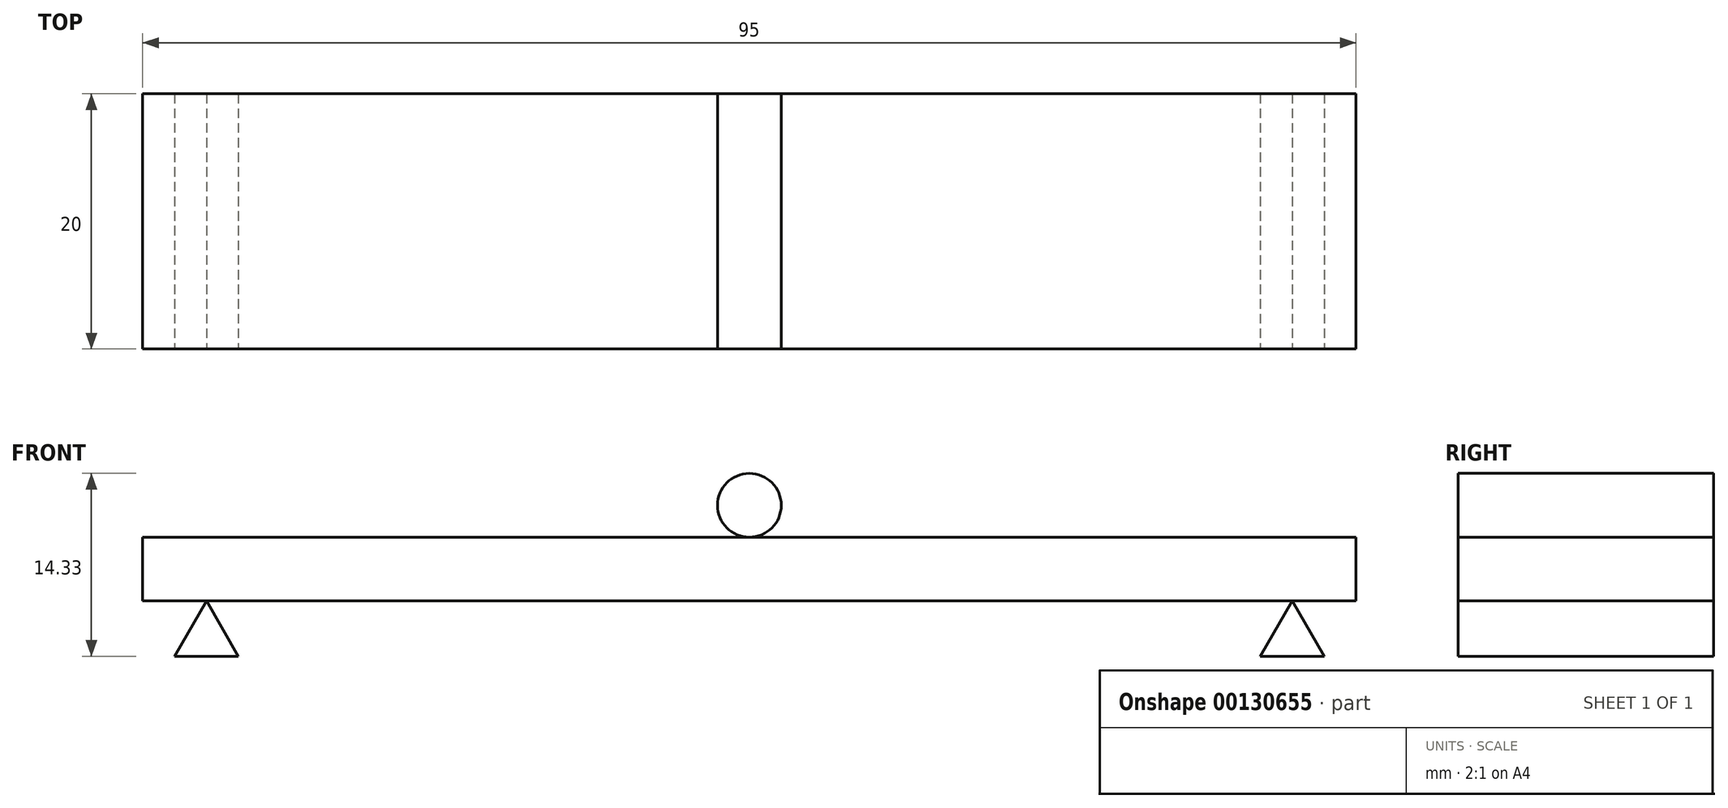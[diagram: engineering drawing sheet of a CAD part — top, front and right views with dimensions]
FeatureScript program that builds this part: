
annotation { "Feature Type Name" : "Feature", "Feature Type Description" : "" }
export const myFeature = defineFeature(function(context is Context, id is Id, definition is map)
    precondition{}
    {
        {
            var Q0;
            Q0=qCreatedBy(makeId("Front.planeOp"),FACE);
            var sketch = newSketch(context, id + "F0", { "sketchPlane" : qUnion([Q0])});
            skLineSegment(sketch, "E0.bottom", {"start": v(47.5, 2.5) * mm, "end": v(-47.5, 2.5) * mm});
            skLineSegment(sketch, "E0.top", {"start": v(47.5, -2.5) * mm, "end": v(-47.5, -2.5) * mm});
            skLineSegment(sketch, "E0.left", {"start": v(47.5, 2.5) * mm, "end": v(47.5, -2.5) * mm});
            skLineSegment(sketch, "E0.right", {"start": v(-47.5, 2.5) * mm, "end": v(-47.5, -2.5) * mm});
            skPoint(sketch, "E0.middle", {"position": v(0, 0) * mm});
            skSolve(sketch);
        }
        {
            var Q0;
            Q0=makeQuery(id+"F0.imprint","IMPRINT",FACE,{"disambiguationData":[TD([[makeQuery(id+"F0.imprint","IMPRINT",EDGE,{"derivedFrom":sQuery(id+"F0.wireOp",EDGE,"E0.bottom")}),1.0]])]});
            extrude(context, id + "F1", {"entities" : qUnion([Q0]), "oppositeDirection" : true, "depth" : 20 * mm});
        }
        {
            var Q0;
            Q0=makeQuery(id+"F1.opExtrude","CAP_FACE",FACE,{"disambiguationData":[OSD([sQuery(id+"F0.wireOp",EDGE,"E0.bottom"),sQuery(id+"F0.wireOp",EDGE,"E0.top"),sQuery(id+"F0.wireOp",EDGE,"E0.left"),sQuery(id+"F0.wireOp",EDGE,"E0.right")])],"isStart":true});
            var sketch = newSketch(context, id + "F2", { "sketchPlane" : qUnion([Q0])});
            skSolve(sketch);
        }
        {
            var Q0;
            Q0=makeQuery(id+"F2.imprint","IMPRINT",FACE,{"disambiguationData":[TD([[makeQuery(id+"F2.imprint","IMPRINT",EDGE,{"derivedFrom":makeQuery(id+"F1.opExtrude","CAP_EDGE",EDGE,{"disambiguationData":[OSD([sQuery(id+"F0.wireOp",EDGE,"E0.bottom")])],"isStart":true})}),1.0]])]});
            var sketch = newSketch(context, id + "F3", { "sketchPlane" : qUnion([Q0])});
            skCircle(sketch, "E1", {"center": v(0, 5) * mm, "radius": 2.5 * mm});
            skSolve(sketch);
        }
        {
            var Q0;
            Q0=makeQuery(id+"F3.imprint","IMPRINT",FACE,{"disambiguationData":[TD([[makeQuery(id+"F3.imprint","IMPRINT",EDGE,{"derivedFrom":sQuery(id+"F3.wireOp",EDGE,"E1")}),1.0]])]});
            extrude(context, id + "F4", {"entities" : qUnion([Q0]), "operationType" : NewBodyOperationType.ADD, "oppositeDirection" : true, "depth" : 20 * mm});
        }
        {
            var Q0;
            Q0=qCreatedBy(makeId("Front.planeOp"),FACE);
            var sketch = newSketch(context, id + "F5", { "sketchPlane" : qUnion([Q0])});
            skLineSegment(sketch, "E2.0", {"start": v(-40, -6.83) * mm, "end": v(-45, -6.83) * mm});
            skLineSegment(sketch, "E2.1", {"start": v(-45, -6.83) * mm, "end": v(-42.5, -2.5) * mm});
            skLineSegment(sketch, "E2.2", {"start": v(-42.5, -2.5) * mm, "end": v(-40, -6.83) * mm});
            skPoint(sketch, "E2.0.midPoint", {"position": v(-42.5, -6.83) * mm});
            skLineSegment(sketch, "E3.0", {"start": v(45, -6.83) * mm, "end": v(40, -6.83) * mm});
            skLineSegment(sketch, "E3.1", {"start": v(40, -6.83) * mm, "end": v(42.5, -2.5) * mm});
            skLineSegment(sketch, "E3.2", {"start": v(42.5, -2.5) * mm, "end": v(45, -6.83) * mm});
            skPoint(sketch, "E3.0.midPoint", {"position": v(42.5, -6.83) * mm});
            skSolve(sketch);
        }
        {
            var Q0;
            Q0=makeQuery(id+"F5.imprint","IMPRINT",FACE,{"disambiguationData":[TD([[makeQuery(id+"F5.imprint","IMPRINT",EDGE,{"derivedFrom":sQuery(id+"F5.wireOp",EDGE,"E2.0")}),-1.0]])]});
            extrude(context, id + "F6", {"entities" : qUnion([Q0]), "oppositeDirection" : true, "depth" : 20 * mm});
        }
        {
            var Q0;
            Q0=makeQuery(id+"F5.imprint","IMPRINT",FACE,{"disambiguationData":[TD([[makeQuery(id+"F5.imprint","IMPRINT",EDGE,{"derivedFrom":sQuery(id+"F5.wireOp",EDGE,"E3.0")}),-1.0]])]});
            extrude(context, id + "F7", {"entities" : qUnion([Q0]), "oppositeDirection" : true, "depth" : 20 * mm});
        }
    });
